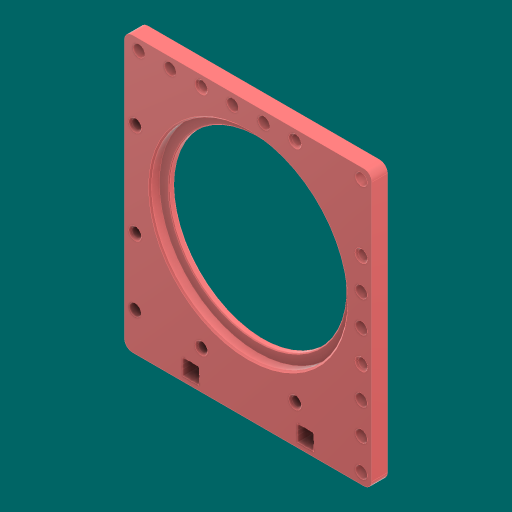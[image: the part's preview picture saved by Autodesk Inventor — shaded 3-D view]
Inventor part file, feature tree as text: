
AUTODESK INVENTOR PART (.ipt)
format: ipt  version: 2023.1 (Build 271208000, 208)  size: 634,368 bytes
history: native  units: in
note: dims shown in document units (in); Inventor stores cm internally (conversion verified against a paired STEP export)
features: chamfer x4, sketch x2, revolve x1, extrude x1, fillet x1
ambient origin geometry x8: Origin, YZ Plane, XZ Plane, XY Plane, X Axis, Y Axis, Z Axis, Center Point
bodies: Solid1 (feature_tree)
feature tree (9):
  revolve  "Revolution1"  [1 undecoded]
  extrude  "Extrusion1"  TaperAngle=360.0deg  [1 undecoded]
  chamfer  "Chamfer1"  Distance=0.1562in
  chamfer  "Chamfer2"  Distance=0.3397in
  chamfer  "Chamfer3"  Distance=3.0in
  chamfer  "Chamfer4"  Distance=1.2in
  fillet  "Fillet1"  Radius=0.26in
  sketch  "Sketch1"  dims[d2=3.1437in d5=0.25in]
  sketch  "Sketch2"  dims[d7=0.2in d8=360.0deg d9=0.1562in d10=0.3397in d16=3.0in d17=1.2in d18=0.26in d19=0.26in d20=0.26in d21=0.26in d24=22.5deg d25=3.1496in d27=360.0deg d29=1.3386in d30=2.2835in d31=1.0in d32=0.27in d35=1.5in d36=0.19in d37=0.5in d38=0.19in d39=1.1811in d41=0.5in d42=0.3937in d44=1.0in d48=0.5in d49=0.19in d50=0.5in d51=0.5in d52=0.7874in d54=0.5in d55=0.3937in d57=1.0in d59=0.25in d60=0.0in d61=0.0236in d62=0.125in d63=45.0deg d64=0.7874in d66=90.0deg d68=0.0236in d69=0.125in d70=45.0deg d71=0.19in d72=3.6in d73=0.33in d74=0.1in d76=0.0118in d77=0.125in d78=45.0deg d79=2.8346in d80=0.0236in d81=0.125in d82=45.0deg d83=0.125in]
note: 2 required parameter values undecoded (feature->parameter linkage not recoverable at this tier; creation-order binding heuristic only, values carry confidence <= 0.55)